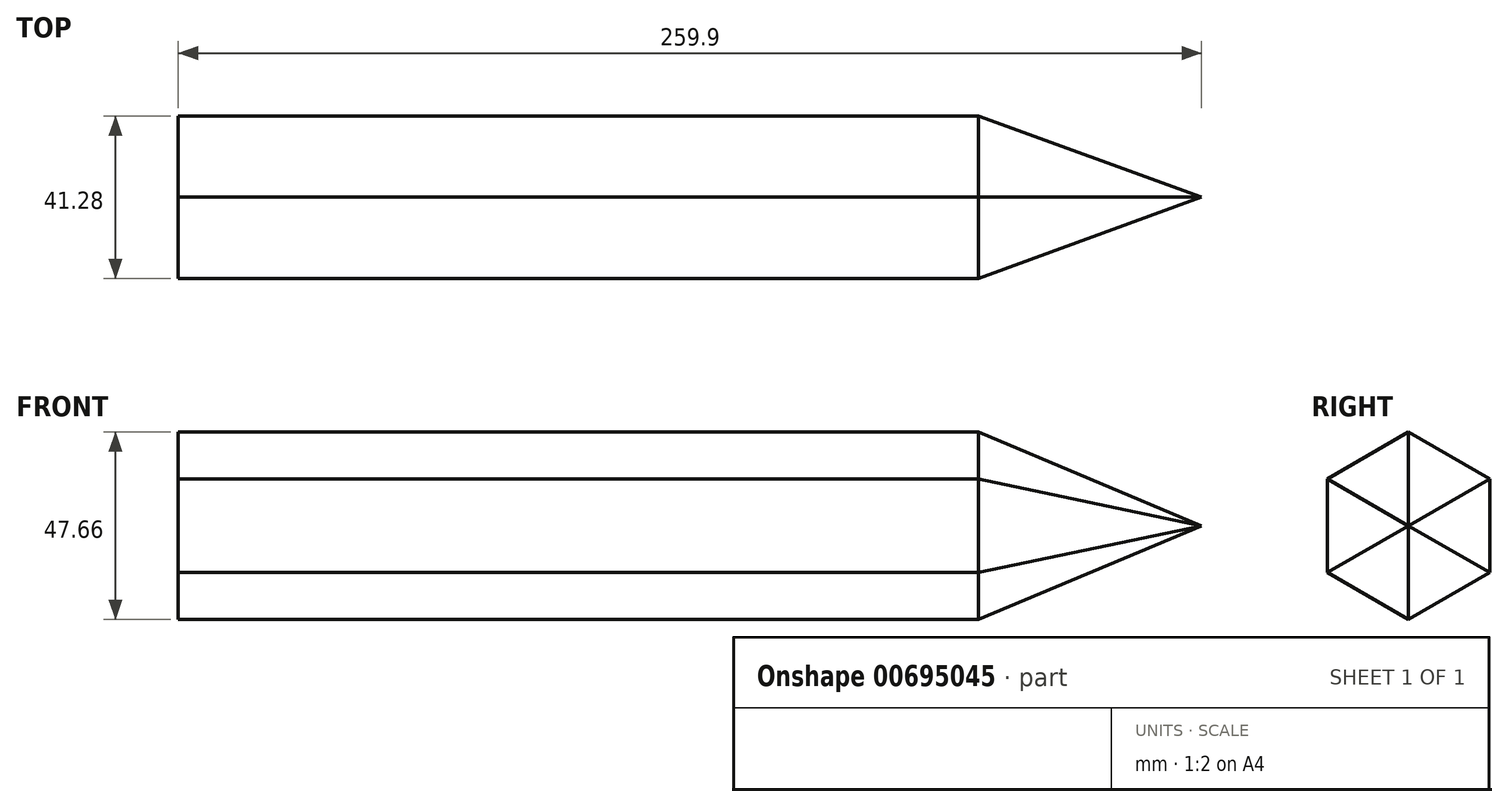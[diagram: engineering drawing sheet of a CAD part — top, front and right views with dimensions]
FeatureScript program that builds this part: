
annotation { "Feature Type Name" : "Feature", "Feature Type Description" : "" }
export const myFeature = defineFeature(function(context is Context, id is Id, definition is map)
    precondition{}
    {
        {
            var Q0;
            Q0=qCreatedBy(makeId("Right.planeOp"),FACE);
            var sketch = newSketch(context, id + "F0", { "sketchPlane" : qUnion([Q0])});
            skCircle(sketch, "E0.cCircle", {"center": v(0, 0) * mm, "radius": 23.83 * mm, "construction": true});
            skLineSegment(sketch, "E0.0", {"start": v(0, 23.83) * mm, "end": v(20.64, 11.92) * mm});
            skLineSegment(sketch, "E0.1", {"start": v(20.64, 11.92) * mm, "end": v(20.64, -11.92) * mm});
            skLineSegment(sketch, "E0.2", {"start": v(20.64, -11.92) * mm, "end": v(0, -23.83) * mm});
            skLineSegment(sketch, "E0.3", {"start": v(0, -23.83) * mm, "end": v(-20.64, -11.92) * mm});
            skLineSegment(sketch, "E0.4", {"start": v(-20.64, -11.92) * mm, "end": v(-20.64, 11.92) * mm});
            skLineSegment(sketch, "E0.5", {"start": v(-20.64, 11.92) * mm, "end": v(0, 23.83) * mm});
            skSolve(sketch);
        }
        {
            var Q0;
            Q0=makeQuery(id+"F0.imprint","IMPRINT",FACE,{"disambiguationData":[TD([[makeQuery(id+"F0.imprint","IMPRINT",EDGE,{"derivedFrom":sQuery(id+"F0.wireOp",EDGE,"E0.0")}),-1.0]])]});
            extrude(context, id + "F1", {"entities" : qUnion([Q0]), "depth" : 203.2 * mm, "offsetDistance" : 25.4 * mm});
        }
        {
            var Q0;
            Q0=makeQuery(id+"F1.opExtrude","CAP_FACE",FACE,{"disambiguationData":[OSD([sQuery(id+"F0.wireOp",EDGE,"E0.0"),sQuery(id+"F0.wireOp",EDGE,"E0.1"),sQuery(id+"F0.wireOp",EDGE,"E0.2"),sQuery(id+"F0.wireOp",EDGE,"E0.3"),sQuery(id+"F0.wireOp",EDGE,"E0.4"),sQuery(id+"F0.wireOp",EDGE,"E0.5")])],"isStart":false});
            var sketch = newSketch(context, id + "F2", { "sketchPlane" : qUnion([Q0])});
            skLineSegment(sketch, "E1.0.0", {"start": v(0, 23.83) * mm, "end": v(-20.64, 11.92) * mm});
            skLineSegment(sketch, "E1.0.1", {"start": v(-20.64, 11.92) * mm, "end": v(-20.64, -11.92) * mm});
            skLineSegment(sketch, "E1.0.2", {"start": v(-20.64, -11.92) * mm, "end": v(0, -23.83) * mm});
            skLineSegment(sketch, "E1.0.3", {"start": v(0, -23.83) * mm, "end": v(20.64, -11.92) * mm});
            skLineSegment(sketch, "E1.0.4", {"start": v(20.64, -11.92) * mm, "end": v(20.64, 11.92) * mm});
            skLineSegment(sketch, "E1.0.5", {"start": v(20.64, 11.92) * mm, "end": v(0, 23.83) * mm});
            skSolve(sketch);
        }
        {
            var Q0;
            Q0=makeQuery(id+"F2.imprint","IMPRINT",FACE,{"disambiguationData":[TD([[makeQuery(id+"F2.imprint","IMPRINT",EDGE,{"derivedFrom":sQuery(id+"F2.wireOp",EDGE,"E1.0.0")}),-1.0]])]});
            extrude(context, id + "F3", {"entities" : qUnion([Q0]), "depth" : 84.84 * mm, "offsetDistance" : 25.4 * mm, "hasDraft" : true, "draftAngle" : 20 * degree, "draftPullDirection" : true});
        }
    });
